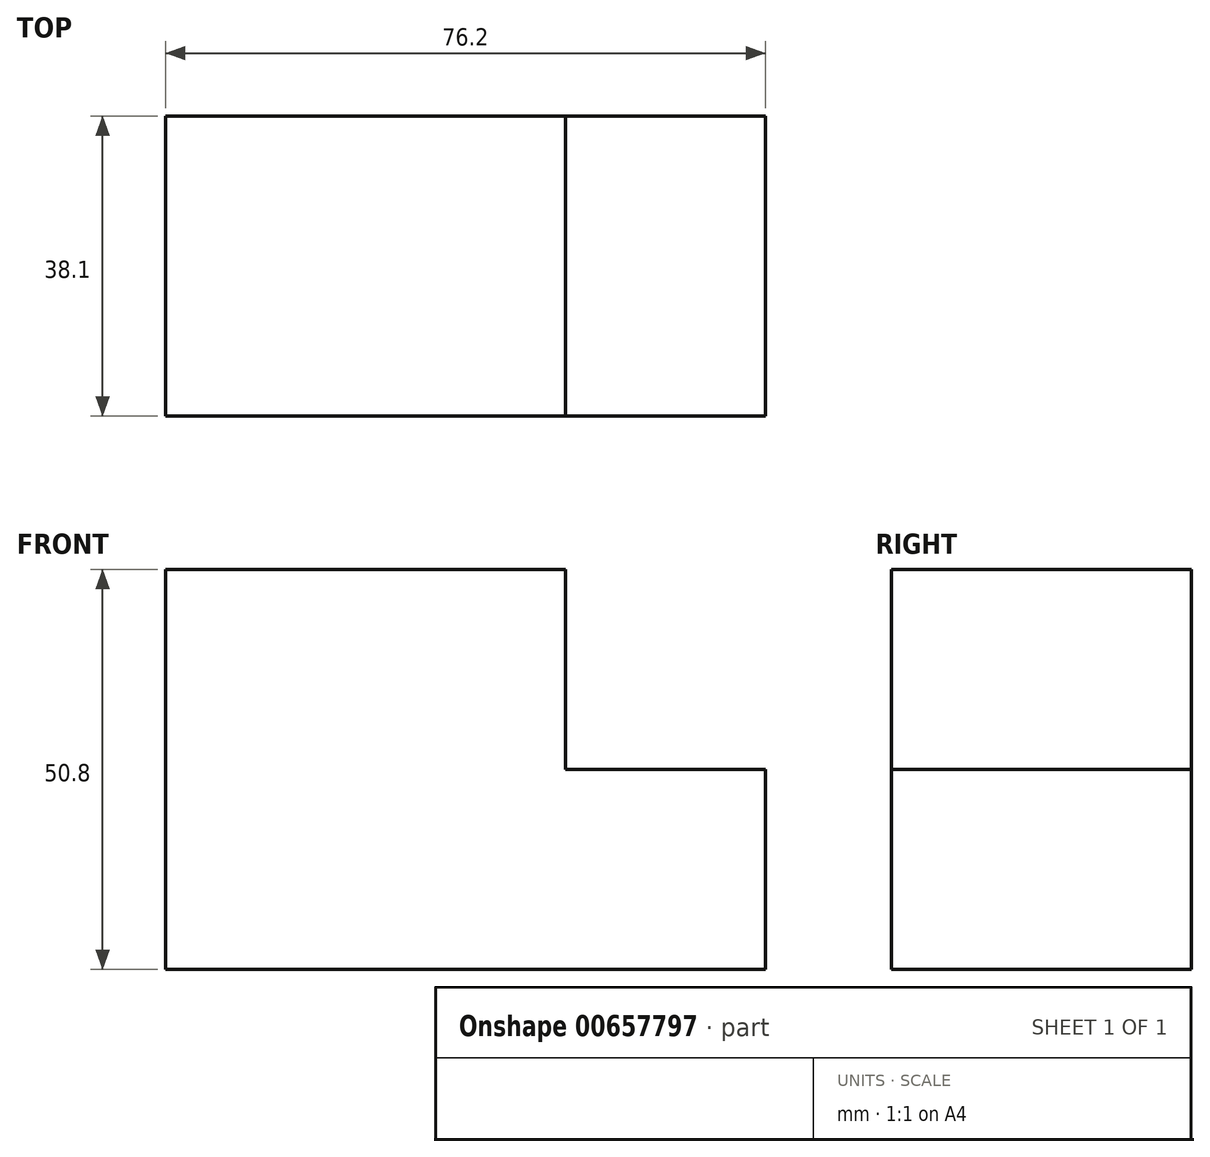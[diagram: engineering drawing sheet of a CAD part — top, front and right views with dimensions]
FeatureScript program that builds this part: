
annotation { "Feature Type Name" : "Feature", "Feature Type Description" : "" }
export const myFeature = defineFeature(function(context is Context, id is Id, definition is map)
    precondition{}
    {
        {
            var Q0;
            Q0=qCreatedBy(makeId("Top.planeOp"),FACE);
            var sketch = newSketch(context, id + "F0", { "sketchPlane" : qUnion([Q0])});
            skLineSegment(sketch, "E0.bottom", {"start": v(-2.97, -11.7) * mm, "end": v(73.23, -11.7) * mm});
            skLineSegment(sketch, "E0.top", {"start": v(-2.97, -49.8) * mm, "end": v(73.23, -49.8) * mm});
            skLineSegment(sketch, "E0.left", {"start": v(-2.97, -11.7) * mm, "end": v(-2.97, -49.8) * mm});
            skLineSegment(sketch, "E0.right", {"start": v(73.23, -11.7) * mm, "end": v(73.23, -49.8) * mm});
            skSolve(sketch);
        }
        {
            var Q0;
            Q0 = qSketchRegion(id + "F0", true);
            extrude(context, id + "F1", {"entities" : qUnion([Q0]), "depth" : 50.8 * mm, "offsetDistance" : 25.4 * mm});
        }
        {
            var Q0;
            Q0=makeQuery(id+"F1.opExtrude","CAP_FACE",FACE,{"disambiguationData":[OSD([sQuery(id+"F0.wireOp",EDGE,"E0.bottom"),sQuery(id+"F0.wireOp",EDGE,"E0.top"),sQuery(id+"F0.wireOp",EDGE,"E0.left"),sQuery(id+"F0.wireOp",EDGE,"E0.right")])],"isStart":false});
            var sketch = newSketch(context, id + "F2", { "sketchPlane" : qUnion([Q0])});
            skLineSegment(sketch, "E1.bottom", {"start": v(27.5, -11.7) * mm, "end": v(41.9, -11.7) * mm});
            skLineSegment(sketch, "E1.top", {"start": v(27.5, -11.7) * mm, "end": v(41.9, -11.7) * mm});
            skLineSegment(sketch, "E1.left", {"start": v(27.5, -11.7) * mm, "end": v(27.5, -11.7) * mm});
            skLineSegment(sketch, "E1.right", {"start": v(41.9, -11.7) * mm, "end": v(41.9, -11.7) * mm});
            skLineSegment(sketch, "E2.bottom", {"start": v(73.23, -11.7) * mm, "end": v(47.83, -11.7) * mm});
            skLineSegment(sketch, "E2.top", {"start": v(73.23, -49.8) * mm, "end": v(47.83, -49.8) * mm});
            skLineSegment(sketch, "E2.left", {"start": v(73.23, -11.7) * mm, "end": v(73.23, -49.8) * mm});
            skLineSegment(sketch, "E2.right", {"start": v(47.83, -11.7) * mm, "end": v(47.83, -49.8) * mm});
            skSolve(sketch);
        }
        {
            var Q0;
            Q0=makeQuery(id+"F2.imprint","IMPRINT",FACE,{"disambiguationData":[TD([[makeQuery(id+"F2.imprint","IMPRINT",EDGE,{"derivedFrom":sQuery(id+"F2.wireOp",EDGE,"E2.bottom")}),-1.0]])]});
            extrude(context, id + "F3", {"entities" : qUnion([Q0]), "operationType" : NewBodyOperationType.REMOVE, "oppositeDirection" : true, "depth" : 25.4 * mm, "offsetDistance" : 25.4 * mm});
        }
    });
